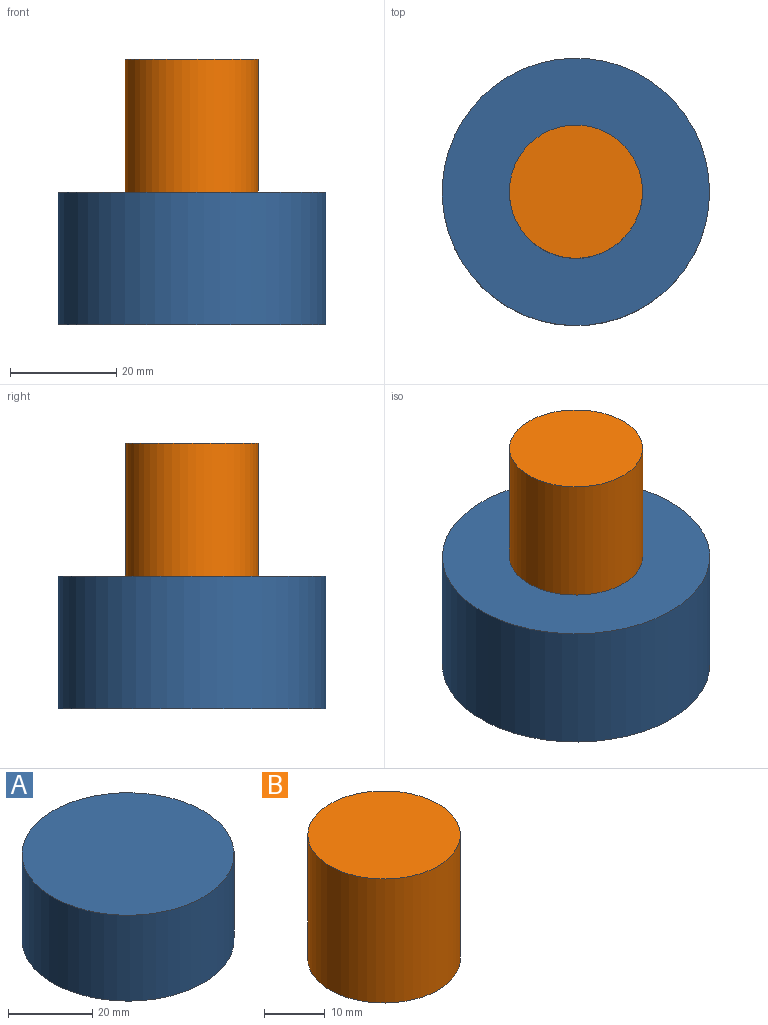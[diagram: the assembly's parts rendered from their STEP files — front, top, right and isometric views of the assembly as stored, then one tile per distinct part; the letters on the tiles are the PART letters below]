
ASSEMBLY  parts=2 mates=1
PART A: 3 faces, bbox 50.4x50.4x25 mm
  f0: cylinder r=25.22mm len=50.44mm, axis (0,0,-1), area 3961.5mm2, adj f1,f2
  f1: plane 50.44x50.44mm, normal (0,0,1), area 1998.1mm2, adj f0
  f2: plane 50.44x50.44mm, normal (0,0,-1), area 1998.1mm2, adj f0
PART B: 3 faces, bbox 25.1x25.1x25 mm
  f0: cylinder r=12.56mm len=25.12mm, axis (0,0,-1), area 1972.6mm2, adj f1,f2
  f1: plane 25.12x25.12mm, normal (0,0,1), area 495.4mm2, adj f0
  f2: plane 25.12x25.12mm, normal (0,0,-1), area 495.4mm2, adj f0
PLACE A t=(-47.09,61.81,-25)mm
PLACE B at identity
MATE fastened A.f0 <-> B.f0  axis (0,0,1) through (-47.09,61.81,0)mm
